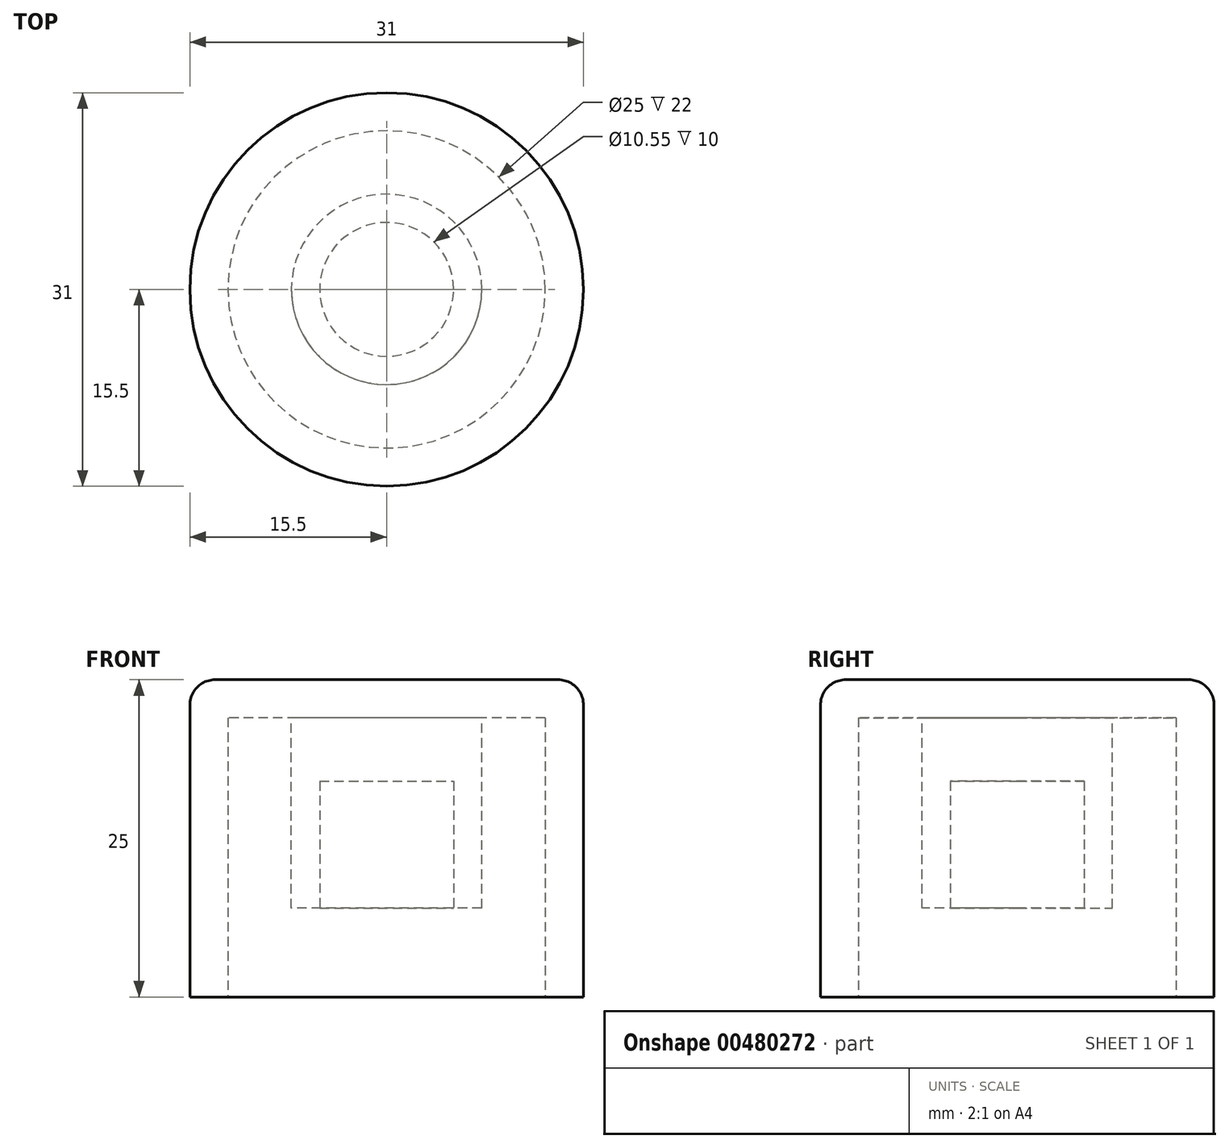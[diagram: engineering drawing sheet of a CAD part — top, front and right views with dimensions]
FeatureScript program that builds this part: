
annotation { "Feature Type Name" : "Feature", "Feature Type Description" : "" }
export const myFeature = defineFeature(function(context is Context, id is Id, definition is map)
    precondition{}
    {
        {
            var Q0;
            Q0=qCreatedBy(makeId("Top.planeOp"),FACE);
            var sketch = newSketch(context, id + "F0", { "sketchPlane" : qUnion([Q0])});
            skCircle(sketch, "E0", {"center": v(0, 0) * mm, "radius": 15.5 * mm});
            skSolve(sketch);
        }
        {
            var Q0;
            Q0 = qSketchRegion(id + "F0", true);
            extrude(context, id + "F1", {"entities" : qUnion([Q0]), "depth" : 25 * mm});
        }
        {
            var Q0;
            Q0=makeQuery(id+"F1.opExtrude","CAP_FACE",FACE,{"disambiguationData":[OSD([sQuery(id+"F0.wireOp",EDGE,"E0")])],"isStart":true});
            shell(context, id + "F2", {"entities" : qUnion([Q0]), "thickness" : 3 * mm});
        }
        {
            var Q0;
            Q0=makeQuery(id+"F1.opExtrude","CAP_EDGE",EDGE,{"disambiguationData":[OSD([sQuery(id+"F0.wireOp",EDGE,"E0")])],"isStart":false});
            fillet(context, id + "F3", {"entities" : qUnion([Q0]), "radius" : 2 * mm, "tangentPropagation" : true, "allowEdgeOverflow" : false});
        }
        {
            var Q0;
            {var subQ0=sQuery(id+"F0.wireOp",EDGE,"E0");Q0=makeQuery(id+"F2.opShell","OFFSET_FACE",FACE,{"disambiguationData":[OSD([subQ0]),TDD([makeQuery(id+"F1.opExtrude","CAP_FACE",FACE,{"disambiguationData":[OSD([subQ0])],"isStart":false})])]});}
            var sketch = newSketch(context, id + "F4", { "sketchPlane" : qUnion([Q0])});
            skCircle(sketch, "E1", {"center": v(0, 0) * mm, "radius": 7.5 * mm});
            skSolve(sketch);
        }
        {
            var Q0;
            Q0 = qSketchRegion(id + "F4", true);
            extrude(context, id + "F5", {"entities" : qUnion([Q0]), "operationType" : NewBodyOperationType.ADD, "depth" : 15 * mm});
        }
        {
            var Q0;
            Q0=makeQuery(id+"F5.opExtrude","CAP_FACE",FACE,{"disambiguationData":[OSD([sQuery(id+"F4.wireOp",EDGE,"E1")])],"isStart":false});
            var sketch = newSketch(context, id + "F6", { "sketchPlane" : qUnion([Q0])});
            skCircle(sketch, "E2", {"center": v(0, 0) * mm, "radius": 5.28 * mm});
            skSolve(sketch);
        }
        {
            var Q0;
            Q0 = qSketchRegion(id + "F6", true);
            extrude(context, id + "F7", {"entities" : qUnion([Q0]), "operationType" : NewBodyOperationType.REMOVE, "oppositeDirection" : true, "depth" : 10 * mm});
        }
    });
